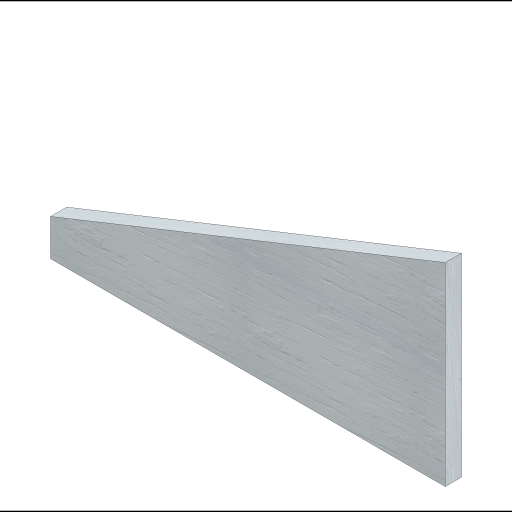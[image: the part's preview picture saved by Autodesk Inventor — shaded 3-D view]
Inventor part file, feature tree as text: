
AUTODESK INVENTOR PART (.ipt)
format: ipt  version: 2023 (Build 270158000, 158)  size: 213,504 bytes
history: native  units: in
note: dims shown in document units (in); Inventor stores cm internally (conversion verified against a paired STEP export)
features: extrude x1, sketch x1
ambient origin geometry x8: Origin, YZ Plane, XZ Plane, XY Plane, X Axis, Y Axis, Z Axis, Center Point
bodies: Solid1 (feature_tree)
feature tree (2):
  extrude  "Extrusion1"  Depth=1.5in
  sketch  "Sketch2"  dims[d5=0.47in d6=1.5in d7=14.0in d8=0.1494in d9=0.47in d10=0.0in]
